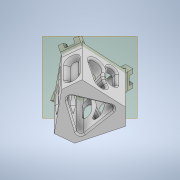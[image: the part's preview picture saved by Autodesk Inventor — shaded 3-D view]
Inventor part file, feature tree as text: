
AUTODESK INVENTOR PART (.ipt)
format: ipt  version: 2020 (Build 240168000, 168)  size: 641,024 bytes
history: native  units: mm
features: sketch x10, extrude x9, thicken_offset x6, fillet x6, projected_geometry x6, pattern_circular x5, other x4, chamfer x3, plane x2, reference x2
ambient origin geometry x8: Origin, YZ Plane, XZ Plane, XY Plane, X Axis, Y Axis, Z Axis, Center Point
bodies: Solid1 (feature_tree)
feature tree (53):
  extrude  "Extrusion1"  Depth=10.0mm
  extrude  "Extrusion2"  Depth=10.0mm
  thicken_offset  "Thicken1"
  thicken_offset  "Thicken2"
  plane  "Work Plane1"
  extrude  "Extrusion3"  Depth=10.0mm
  pattern_circular  "Circular Pattern1"  [2 undecoded]
  plane  "Work Plane2"
  extrude  "Extrusion4"  Depth=2.5mm TaperAngle=360.0deg
  fillet  "Fillet1"  Radius=5.0mm
  fillet  "Fillet2"  Radius=2.0mm
  fillet  "Fillet3"  Radius=4.0mm
  extrude  "Extrusion5"  Depth=2.5mm
  sketch  "Sketch6"  dims[d10=3.0mm]
  fillet  "Fillet4"  Radius=55.0mm
  extrude  "Extrusion6"  Depth=2.5mm
  pattern_circular  "Circular Pattern2"  [2 undecoded]
  extrude  "Extrusion7"  Depth=2.5mm TaperAngle=360.0deg
  pattern_circular  "Circular Pattern3"  [2 undecoded]
  chamfer  "Chamfer1"  Distance=30.0mm Angle=360.0deg
  extrude  "Extrusion9"  Depth=2.5mm TaperAngle=45.0deg
  chamfer  "Chamfer2"  Distance=12.0mm
  pattern_circular  "Circular Pattern4"  [2 undecoded]
  chamfer  "Chamfer3"  Distance=5.0mm
  extrude  "Extrusion10"  Depth=2.5mm TaperAngle=45.0deg
  pattern_circular  "Circular Pattern5"  Count=3 Angle=360.0deg
  thicken_offset  "Thicken3"
  thicken_offset  "Thicken4"
  thicken_offset  "Thicken5"
  fillet  "Fillet5"  Radius=5.0mm
  thicken_offset  "Thicken6"
  fillet  "Fillet6"  Radius=4.0mm
  sketch  "Sketch1"  dims[d0=10.0mm d1=16.0mm]
  reference  "Reference1"
  sketch  "Sketch2"  dims[d2=5.0mm d3=0.0mm d4=10.0mm]
  projected_geometry  "Projected Loop1"
  sketch  "Sketch3"  dims[d5=2.5mm d6=10.0mm]
  reference  "Reference2"
  sketch  "Sketch4"  dims[d7=2.5mm]
  sketch  "Sketch5"  dims[d8=5.0mm d9=0.0mm]
  projected_geometry  "Projected Loop2"
  projected_geometry  "Projected Loop3"
  sketch  "Sketch7"  dims[d11=3.0mm]
  projected_geometry  "Projected Loop4"
  sketch  "Sketch8"  dims[d12=3.0mm]
  sketch  "Sketch9"  dims[d13=3.0mm]
  projected_geometry  "Projected Loop5"
  sketch  "Sketch10"  dims[d14=3.0mm d15=5.0mm d16=0.0mm d17=30.0mm d18=360.0deg d20=5.0mm d21=0.0mm d22=2.0mm d23=4.0mm d24=3.0mm d25=55.0mm d26=0.0mm d27=8.0mm d28=55.0mm d29=0.0mm d30=30.0mm d31=360.0deg d33=55.0mm d34=0.0mm d35=30.0mm d36=360.0deg d38=2.0mm d39=2.0mm d40=45.0deg d43=12.0mm d44=8.0mm d45=5.0mm d46=0.0mm d47=5.0mm d48=2.0mm d49=45.0deg d50=30.0mm d51=360.0deg d53=5.0mm d54=2.0mm d55=45.0deg d56=4.0mm d57=5.0mm d58=20.0mm d59=0.0mm d60=30.0mm d61=360.0deg d63=2.0mm d64=2.0mm d65=2.0mm d66=2.0mm d67=2.0mm d68=2.0mm d69=12.0mm d70=10.0mm d71=10.0mm d72=2.5mm]
  projected_geometry  "Projected Loop6"
  parser-record x1  (decoder bookkeeping rows leaked as tree rows — omitted from the tree; the rows remain in map.json)
  other  "delta_1.iam"
  other  "arm_holder_2:2"
  other  "arm_holder_1:1"
note: 8 required parameter values undecoded (feature->parameter linkage not recoverable at this tier; creation-order binding heuristic only, values carry confidence <= 0.55)
note: 1 file-system path scrubbed to <path> (originals preserved in map.json)
